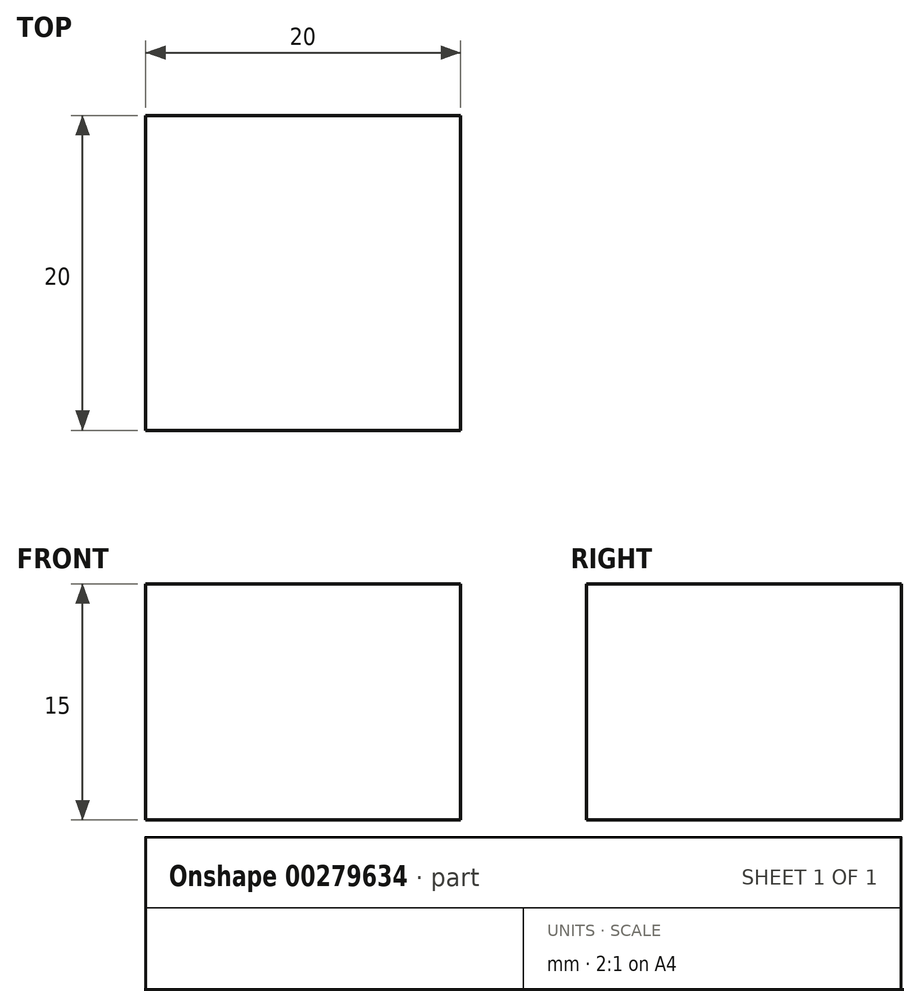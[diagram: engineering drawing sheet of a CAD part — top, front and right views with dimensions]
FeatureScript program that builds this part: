
annotation { "Feature Type Name" : "Feature", "Feature Type Description" : "" }
export const myFeature = defineFeature(function(context is Context, id is Id, definition is map)
    precondition{}
    {
        {
            var Q0;
            Q0=qCreatedBy(makeId("Front.planeOp"),FACE);
            var sketch = newSketch(context, id + "F0", { "sketchPlane" : qUnion([Q0])});
            skLineSegment(sketch, "E0.bottom", {"start": v(0, 0) * mm, "end": v(20, 0) * mm});
            skLineSegment(sketch, "E0.top", {"start": v(0, 15) * mm, "end": v(20, 15) * mm});
            skLineSegment(sketch, "E0.left", {"start": v(0, 0) * mm, "end": v(0, 15) * mm});
            skLineSegment(sketch, "E0.right", {"start": v(20, 0) * mm, "end": v(20, 15) * mm});
            skSolve(sketch);
        }
        {
            var Q0;
            Q0 = qSketchRegion(id + "F0", true);
            extrude(context, id + "F1", {"entities" : qUnion([Q0]), "depth" : 20 * mm});
        }
    });
